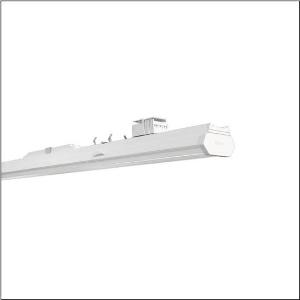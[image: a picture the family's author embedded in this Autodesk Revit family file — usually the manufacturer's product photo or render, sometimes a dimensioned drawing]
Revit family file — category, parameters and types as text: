
# Revit family: licross_r__21_protected_mo_52td12dn4a5g_44fa
name_source: partatom
category: Lighting Fixtures
units: mm (PartAtom-declared; Revit-internal decimal feet)

## family parameters
Cut with Voids When Loaded = No
Host = Face
Light Source = No
Part Type = Normal
Room Calculation Point = No
Round Connector Dimension = Use Diameter
Shared = No

## types (1)
- --- (1 x LED, 10700 lm, 62 W, 4000K)
    Apparent Load = 62 VA
    CIE Flux Codes = 73 92 98 99 100
    Color Rendering = 80
    Color Temperature = 4000K
    Default Elevation = 1800 mm
    Description = Licross® 21 Protected MO, luminaire insert, of sheet steel, galvanised, coil coated, white, length: 1.500mm, width: 90mm, height: 103mm, LED rated luminous flux: 10.700lm, light colour: 840, control gear: DALI 2, with plug, 5-pole, with phase selection, mains connection: 220..240V, AC, 50/60Hz, rated input power: 62W, halogen-free wiring, primary light control with lens, of plastic, primary optical cover: cover, of PMMA, light emission: direct distribution, primary light characteristic: symmetric, protection rating (complete): IP54, insulation class (complete): insulation class I (protective earthing), certification: CE, ENEC, VDE, UKCA, protection symbol: D if used in an environment with non-conductive dust loads with corresponding accessories, impact resistance: IK06, permissible ambient temperature for indoor applications: -25..+35°C, corresponds to IFS (International Featured Standards) requirements for safety and quality in the food industry, reducing of maximum allowable ambient temperature of 5°C with ceiling mounting, LABS conformity tested according to VDMA 24364:2018-05, packaging unit: 1 piece
    Height = 92 mm
    Lamp = 1 x LED
    Lamp Light Flux = 10700 lm
    Lamp Power = 62 W
    Lamp count = 1
    Length = 1500 mm
    Luminous efficacy = 173 lm/W
    Manufacturer = Siteco
    ModVariant = No
    Model = 52TD12DN4A5G
    Mounting Place = Ceiling
    Mounting Type = Pendant
    Number of Poles = 1
    OnlyDefault = Yes
    Power Factor = 1
    Product Name = Licross® 21 Protected MO
    Product group = luminaire insert
    ProductGroupID = 901
    Protection Class = Protection class I
    Protection Degree = IP 54
    RLX_Detail_Level = 1
    RLX_Emergency_Light_Flux = 0 lm
    RLX_Emergency_Type = 0
    RLX_Emergency_Type_DB = No
    RlxData = <blob elided: 24461 chars, md5=b6afea77>
    Socket = socket
    Standby Power = 0 W
    System Light Flux = 10700 lm
    System Power = 62 W
    Type Comments = factory setting: luminous flux: 100 % | dim-lin: 254 | 418 mA
    Type Image = l_1256148.jpg
    URL = http://relux.com
    VarID = @adj_060373
    Voltage = 0 V
    Weight = 0.00 kg
    Width = 88 mm

## geometry (parser evidence)
native form markers: Blend x4, Sweep x11
no freeform markers — native parametric forms only
